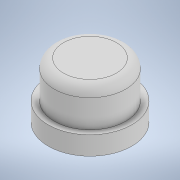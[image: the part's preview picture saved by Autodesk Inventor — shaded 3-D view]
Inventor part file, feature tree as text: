
AUTODESK INVENTOR PART (.ipt)
format: ipt  version: 2022 (Build 260153000, 153)  size: 132,608 bytes
history: native  units: mm
features: extrude x3, sketch x3, fillet x1
ambient origin geometry x8: Origin, YZ Plane, XZ Plane, XY Plane, X Axis, Y Axis, Z Axis, Center Point
bodies: Solid1 (feature_tree)
feature tree (7):
  extrude  "Extrusion1"  Depth=4.0mm TaperAngle=0.0deg
  fillet  "Fillet1"  Radius=1.0mm
  extrude  "Extrusion2"  Depth=2.0mm TaperAngle=0.0deg
  extrude  "Extrusion3"  Depth=2.0mm TaperAngle=0.0deg
  sketch  "Sketch1"  dims[d0=7.7mm d1=4.0mm d2=0.0mm d3=1.0mm]
  sketch  "Sketch2"  dims[d4=9.0mm d5=2.0mm d6=0.0mm]
  sketch  "Sketch3"  dims[d7=4.2mm d8=2.0mm d9=0.0mm]
